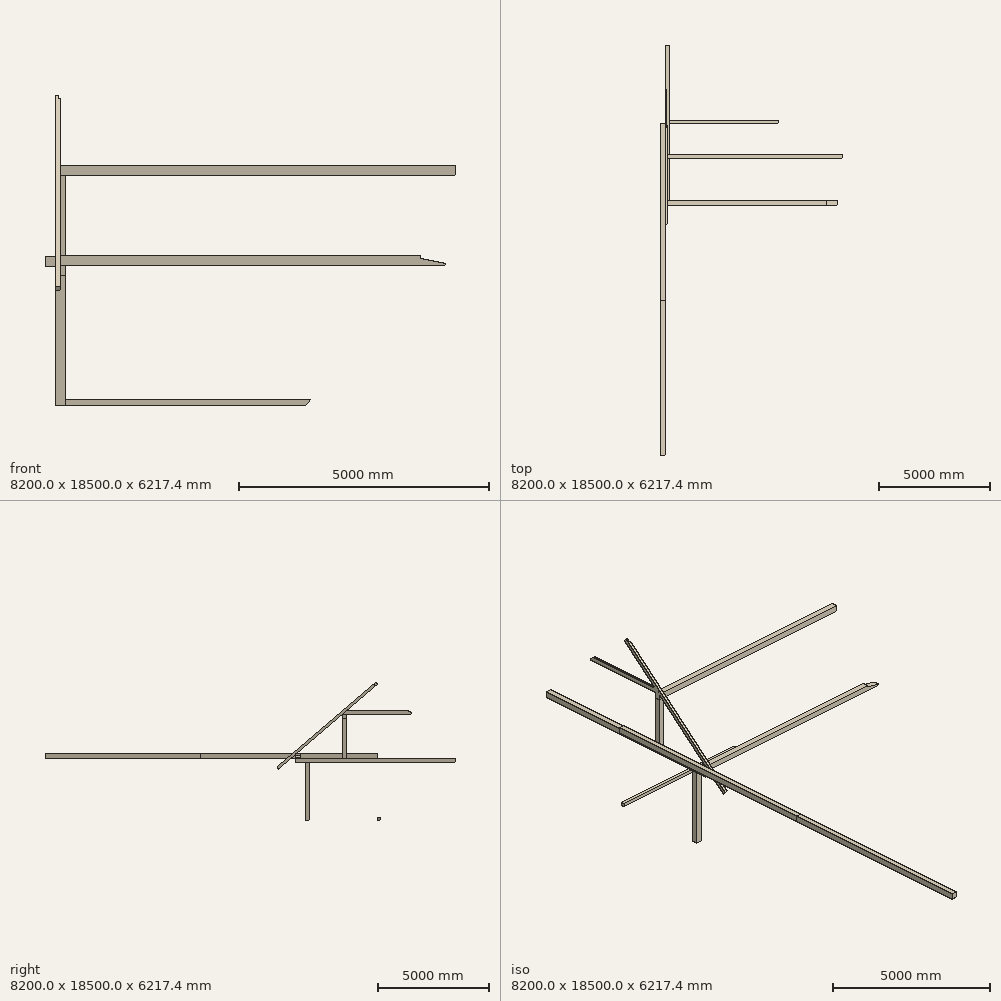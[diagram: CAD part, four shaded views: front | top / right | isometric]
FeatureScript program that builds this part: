
annotation { "Feature Type Name" : "Feature", "Feature Type Description" : "" }
export const myFeature = defineFeature(function(context is Context, id is Id, definition is map)
    precondition{}
    {
        {
            var Q0;
            Q0=qCreatedBy(makeId("Top.planeOp"),FACE);
            var sketch = newSketch(context, id + "F0", { "sketchPlane" : qUnion([Q0])});
            skLineSegment(sketch, "E0.bottom", {"start": v(7000, 3300) * mm, "end": v(-7000, 3300) * mm});
            skLineSegment(sketch, "E0.top", {"start": v(7000, -3300) * mm, "end": v(-7000, -3300) * mm});
            skLineSegment(sketch, "E0.left", {"start": v(7000, 3300) * mm, "end": v(7000, -3300) * mm});
            skLineSegment(sketch, "E0.right", {"start": v(-7000, 3300) * mm, "end": v(-7000, -3300) * mm});
            skPoint(sketch, "E0.middle", {"position": v(0, 0) * mm});
            skSolve(sketch);
        }
        {
            var Q0;
            Q0=qCreatedBy(makeId("Right.planeOp"),FACE);
            var sketch = newSketch(context, id + "F1", { "sketchPlane" : qUnion([Q0])});
            skLineSegment(sketch, "E1", {"start": v(-3286.48, 0) * mm, "end": v(-3286.48, 2600) * mm});
            skLineSegment(sketch, "E2", {"start": v(-3286.48, 2600) * mm, "end": v(-3086.48, 2600) * mm});
            skLineSegment(sketch, "E3", {"start": v(-3086.48, 2600) * mm, "end": v(-3086.48, 0) * mm});
            skLineSegment(sketch, "E4", {"start": v(-3086.48, 0) * mm, "end": v(-3286.48, 0) * mm});
            skSolve(sketch);
        }
        {
            var Q0;
            Q0=makeQuery(id+"F1.imprint","IMPRINT",FACE,{"disambiguationData":[TD([[makeQuery(id+"F1.imprint","IMPRINT",EDGE,{"derivedFrom":sQuery(id+"F1.wireOp",EDGE,"E1")}),-1.0]])]});
            extrude(context, id + "F2", {"entities" : qUnion([Q0]), "depth" : 200 * mm, "offsetDistance" : 25 * mm});
        }
        {
            var Q0;
            Q0=qCreatedBy(makeId("Front.planeOp"),FACE);
            var sketch = newSketch(context, id + "F3", { "sketchPlane" : qUnion([Q0])});
            skLineSegment(sketch, "E5.bottom", {"start": v(-200, 2997.5) * mm, "end": v(0, 2997.5) * mm});
            skLineSegment(sketch, "E5.top", {"start": v(-200, 2797.5) * mm, "end": v(0, 2797.5) * mm});
            skLineSegment(sketch, "E5.left", {"start": v(-200, 2997.5) * mm, "end": v(-200, 2797.5) * mm});
            skLineSegment(sketch, "E5.right", {"start": v(0, 2997.5) * mm, "end": v(0, 2797.5) * mm});
            skSolve(sketch);
        }
        {
            var Q0;
            Q0 = qSketchRegion(id + "F3", true);
            extrude(context, id + "F4", {"entities" : qUnion([Q0]), "depth" : 8000 * mm, "offsetDistance" : 25 * mm});
        }
        {
            var Q0;
            Q0=qCreatedBy(makeId("Right.planeOp"),FACE);
            var sketch = newSketch(context, id + "F5", { "sketchPlane" : qUnion([Q0])});
            skLineSegment(sketch, "E6.bottom", {"start": v(-3700, 0) * mm, "end": v(3500, 0) * mm});
            skLineSegment(sketch, "E6.top", {"start": v(-3700, 2600) * mm, "end": v(3500, 2600) * mm});
            skLineSegment(sketch, "E6.left", {"start": v(-3700, 0) * mm, "end": v(-3700, 2600) * mm});
            skLineSegment(sketch, "E6.right", {"start": v(3500, 0) * mm, "end": v(3500, 2600) * mm});
            skLineSegment(sketch, "E7", {"start": v(-4500, 1914.29) * mm, "end": v(-100, 5685.71) * mm});
            skLineSegment(sketch, "E8", {"start": v(-100, 5685.71) * mm, "end": v(4300, 1914.29) * mm});
            skPoint(sketch, "E9", {"position": v(-100, 2600) * mm});
            skLineSegment(sketch, "E10.top", {"start": v(-3700, 3000) * mm, "end": v(3500, 3000) * mm});
            skLineSegment(sketch, "E10.left", {"start": v(-3700, 2600) * mm, "end": v(-3700, 3000) * mm});
            skLineSegment(sketch, "E10.right", {"start": v(3500, 2600) * mm, "end": v(3500, 3000) * mm});
            skLineSegment(sketch, "E11", {"start": v(-4500, 2314.29) * mm, "end": v(-100, 6085.71) * mm});
            skLineSegment(sketch, "E12", {"start": v(-100, 6085.71) * mm, "end": v(4300, 2314.29) * mm});
            skLineSegment(sketch, "E13.bottom", {"start": v(-1600, 4800) * mm, "end": v(1400, 4800) * mm});
            skLineSegment(sketch, "E13.top", {"start": v(-1600, 2800) * mm, "end": v(1400, 2800) * mm});
            skLineSegment(sketch, "E13.left", {"start": v(-1600, 4800) * mm, "end": v(-1600, 2800) * mm});
            skLineSegment(sketch, "E13.right", {"start": v(1400, 4800) * mm, "end": v(1400, 2800) * mm});
            skPoint(sketch, "E14", {"position": v(-100, 2800) * mm});
            skSolve(sketch);
        }
        {
            var Q0;
            Q0=makeQuery(id+"F4.opExtrude","CAP_FACE",FACE,{"disambiguationData":[OSD([sQuery(id+"F3.wireOp",EDGE,"E5.bottom"),sQuery(id+"F3.wireOp",EDGE,"E5.top"),sQuery(id+"F3.wireOp",EDGE,"E5.left"),sQuery(id+"F3.wireOp",EDGE,"E5.right")])],"isStart":false});
            extrude(context, id + "F6", {"entities" : qUnion([Q0]), "depth" : 7000 * mm, "offsetDistance" : 25 * mm});
        }
        {
            var Q0;
            Q0=qCreatedBy(makeId("Right.planeOp"),FACE);
            var sketch = newSketch(context, id + "F7", { "sketchPlane" : qUnion([Q0])});
            skLineSegment(sketch, "E15.bottom", {"start": v(0, 0) * mm, "end": v(120, 0) * mm});
            skLineSegment(sketch, "E15.top", {"start": v(0, 120) * mm, "end": v(120, 120) * mm});
            skLineSegment(sketch, "E15.left", {"start": v(0, 0) * mm, "end": v(0, 120) * mm});
            skLineSegment(sketch, "E15.right", {"start": v(120, 0) * mm, "end": v(120, 120) * mm});
            skSolve(sketch);
        }
        {
            var Q0;
            Q0 = qSketchRegion(id + "F7", true);
            extrude(context, id + "F8", {"entities" : qUnion([Q0]), "depth" : 5100 * mm, "offsetDistance" : 25 * mm});
        }
        {
            var Q0;
            Q0=makeQuery(id+"F8.opExtrude","SWEPT_FACE",FACE,{"disambiguationData":[OSD([sQuery(id+"F7.wireOp",EDGE,"E15.right")])]});
            var sketch = newSketch(context, id + "F9", { "sketchPlane" : qUnion([Q0])});
            skLineSegment(sketch, "E16", {"start": v(-5100, 120) * mm, "end": v(-5015.98, 0) * mm});
            skSolve(sketch);
        }
        {
            var Q0;
            {var subQ0=sQuery(id+"F9.wireOp",EDGE,"E16");Q0=makeQuery(id+"F9.imprint","IMPRINT",FACE,{"disambiguationData":[TD([[makeQuery(id+"F9.imprint","IMPRINT",EDGE,{"derivedFrom":subQ0}),-1.0]])]});}
            extrude(context, id + "F10", {"entities" : qUnion([Q0]), "operationType" : NewBodyOperationType.REMOVE, "endBound" : BoundingType.THROUGH_ALL, "oppositeDirection" : true, "depth" : 25 * mm, "offsetDistance" : 25 * mm});
        }
        {
            var Q0;
            Q0=qCreatedBy(makeId("Right.planeOp"),FACE);
            var sketch = newSketch(context, id + "F11", { "sketchPlane" : qUnion([Q0])});
            skLineSegment(sketch, "E17.0", {"start": v(-4486.98, 1899.1) * mm, "end": v(-84.63, 5672.54) * mm});
            skLineSegment(sketch, "E18.0", {"start": v(-4565.08, 1990.21) * mm, "end": v(-176.83, 5751.57) * mm, "construction": true});
            skLineSegment(sketch, "E19", {"start": v(-4565.08, 1990.21) * mm, "end": v(-4486.98, 1899.1) * mm});
            skLineSegment(sketch, "E20", {"start": v(-176.83, 5751.57) * mm, "end": v(-84.63, 5672.54) * mm, "construction": true});
            skPoint(sketch, "E21.0", {"position": v(-3700, 2600) * mm});
            skLineSegment(sketch, "E22", {"start": v(-3700, 2600) * mm, "end": v(-3700, 2573.66) * mm});
            skLineSegment(sketch, "E23", {"start": v(-3700, 2600) * mm, "end": v(-3669.27, 2600) * mm});
            skLineSegment(sketch, "E24", {"start": v(-100, 5817.42) * mm, "end": v(-7.8, 5738.4) * mm});
            skLineSegment(sketch, "E25", {"start": v(-176.83, 5751.57) * mm, "end": v(-100, 5817.42) * mm});
            skLineSegment(sketch, "E26", {"start": v(-7.8, 5738.4) * mm, "end": v(-84.63, 5672.54) * mm});
            skLineSegment(sketch, "E27.0", {"start": v(-4486.98, 2299.1) * mm, "end": v(-7.8, 6138.4) * mm});
            skLineSegment(sketch, "E28.0", {"start": v(-4565.08, 2390.21) * mm, "end": v(-100, 6217.42) * mm});
            skLineSegment(sketch, "E29", {"start": v(-4565.08, 2390.21) * mm, "end": v(-4486.98, 2299.1) * mm});
            skLineSegment(sketch, "E30", {"start": v(-100, 6217.42) * mm, "end": v(-7.8, 6138.4) * mm});
            skPoint(sketch, "E31.0", {"position": v(-3700, 3000) * mm});
            skLineSegment(sketch, "E32", {"start": v(-3700, 3000) * mm, "end": v(-3669.27, 3000) * mm});
            skLineSegment(sketch, "E33", {"start": v(-3700, 3000) * mm, "end": v(-3700, 2973.66) * mm});
            skSolve(sketch);
        }
        {
            var Q0;
            Q0=makeQuery(id+"F11.imprint","IMPRINT",FACE,{"disambiguationData":[TD([[makeQuery(id+"F11.imprint","IMPRINT",EDGE,{"derivedFrom":sQuery(id+"F11.wireOp",EDGE,"E28.0")}),-1.0]])]});
            extrude(context, id + "F12", {"entities" : qUnion([Q0]), "depth" : 100 * mm, "offsetDistance" : 25 * mm});
        }
        {
            var Q0;
            Q0=makeQuery(id+"F12.opExtrude","CAP_FACE",FACE,{"disambiguationData":[OSD([sQuery(id+"F11.wireOp",EDGE,"E27.0"),sQuery(id+"F11.wireOp",EDGE,"E28.0"),sQuery(id+"F11.wireOp",EDGE,"E29"),sQuery(id+"F11.wireOp",EDGE,"E30"),sQuery(id+"F11.wireOp",EDGE,"E32"),sQuery(id+"F11.wireOp",EDGE,"E33")])],"isStart":false});
            var sketch = newSketch(context, id + "F13", { "sketchPlane" : qUnion([Q0])});
            skLineSegment(sketch, "E34", {"start": v(-192.2, 6138.4) * mm, "end": v(-100, 6059.37) * mm});
            skSolve(sketch);
        }
        {
            var Q0;
            {var subQ0=sQuery(id+"F13.wireOp",EDGE,"E34");Q0=makeQuery(id+"F13.imprint","IMPRINT",FACE,{"disambiguationData":[TD([[makeQuery(id+"F13.imprint","IMPRINT",EDGE,{"derivedFrom":subQ0}),1.0]])]});}
            extrude(context, id + "F14", {"entities" : qUnion([Q0]), "operationType" : NewBodyOperationType.REMOVE, "oppositeDirection" : true, "depth" : 50 * mm, "offsetDistance" : 25 * mm});
        }
        {
            var Q0;
            Q0=qCreatedBy(makeId("Right.planeOp"),FACE);
            var sketch = newSketch(context, id + "F15", { "sketchPlane" : qUnion([Q0])});
            skPoint(sketch, "E35.0", {"position": v(-3700, 2600) * mm});
            skPoint(sketch, "E35.1", {"position": v(3500, 2600) * mm});
            skLineSegment(sketch, "E36.bottom", {"start": v(-3700, 2600) * mm, "end": v(3500, 2600) * mm});
            skLineSegment(sketch, "E36.top", {"start": v(-3700, 2800) * mm, "end": v(3500, 2800) * mm});
            skLineSegment(sketch, "E36.left", {"start": v(-3700, 2600) * mm, "end": v(-3700, 2800) * mm});
            skLineSegment(sketch, "E36.right", {"start": v(3500, 2600) * mm, "end": v(3500, 2800) * mm});
            skSolve(sketch);
        }
        {
            var Q0;
            Q0 = qSketchRegion(id + "F15", true);
            extrude(context, id + "F16", {"entities" : qUnion([Q0]), "depth" : 200 * mm, "offsetDistance" : 25 * mm});
        }
        {
            var Q0;
            Q0=qCreatedBy(makeId("Right.planeOp"),FACE);
            var sketch = newSketch(context, id + "F17", { "sketchPlane" : qUnion([Q0])});
            skPoint(sketch, "E37.0", {"position": v(-3700, 2800) * mm});
            skLineSegment(sketch, "E38.bottom", {"start": v(-3700, 2800) * mm, "end": v(-3500, 2800) * mm});
            skLineSegment(sketch, "E38.top", {"start": v(-3700, 3000) * mm, "end": v(-3500, 3000) * mm});
            skLineSegment(sketch, "E38.left", {"start": v(-3700, 2800) * mm, "end": v(-3700, 3000) * mm});
            skLineSegment(sketch, "E38.right", {"start": v(-3500, 2800) * mm, "end": v(-3500, 3000) * mm});
            skSolve(sketch);
        }
        {
            var Q0;
            Q0 = qSketchRegion(id + "F17", true);
            extrude(context, id + "F18", {"entities" : qUnion([Q0]), "depth" : 7800 * mm, "offsetDistance" : 25 * mm});
        }
        {
            var Q0;
            Q0=makeQuery(id+"F18.opExtrude","SWEPT_FACE",FACE,{"disambiguationData":[OSD([sQuery(id+"F17.wireOp",EDGE,"E38.left")])]});
            var sketch = newSketch(context, id + "F19", { "sketchPlane" : qUnion([Q0])});
            skLineSegment(sketch, "E39", {"start": v(7800, 2800) * mm, "end": v(7800, 2850) * mm});
            skLineSegment(sketch, "E40", {"start": v(7800, 2850) * mm, "end": v(7300, 2950) * mm});
            skLineSegment(sketch, "E41", {"start": v(7300, 2950) * mm, "end": v(7300, 3000) * mm});
            skSolve(sketch);
        }
        {
            var Q0;
            {var subQ0=sQuery(id+"F19.wireOp",EDGE,"E40");Q0=makeQuery(id+"F19.imprint","IMPRINT",FACE,{"disambiguationData":[TD([[makeQuery(id+"F19.imprint","IMPRINT",EDGE,{"derivedFrom":subQ0}),-1.0]])]});}
            extrude(context, id + "F20", {"entities" : qUnion([Q0]), "operationType" : NewBodyOperationType.REMOVE, "endBound" : BoundingType.THROUGH_ALL, "oppositeDirection" : true, "depth" : 25 * mm, "offsetDistance" : 25 * mm});
        }
        {
            var Q0;
            Q0=qCreatedBy(makeId("Right.planeOp"),FACE);
            var sketch = newSketch(context, id + "F21", { "sketchPlane" : qUnion([Q0])});
            skLineSegment(sketch, "E42.0", {"start": v(-3700, 3000) * mm, "end": v(3500, 3000) * mm});
            skLineSegment(sketch, "E43.0", {"start": v(-3669.27, 3000) * mm, "end": v(-100, 6059.37) * mm});
            skLineSegment(sketch, "E44", {"start": v(-1335.93, 3000) * mm, "end": v(-1335.93, 5000) * mm});
            skLineSegment(sketch, "E45.0", {"start": v(-3700, 2800) * mm, "end": v(3500, 2800) * mm});
            skLineSegment(sketch, "E46", {"start": v(-1569.27, 2800) * mm, "end": v(-1569.27, 4800) * mm});
            skSolve(sketch);
        }
        {
            var Q0;
            Q0=makeQuery(id+"F12.opExtrude","CAP_FACE",FACE,{"disambiguationData":[OSD([sQuery(id+"F11.wireOp",EDGE,"E27.0"),sQuery(id+"F11.wireOp",EDGE,"E28.0"),sQuery(id+"F11.wireOp",EDGE,"E29"),sQuery(id+"F11.wireOp",EDGE,"E30"),sQuery(id+"F11.wireOp",EDGE,"E32"),sQuery(id+"F11.wireOp",EDGE,"E33")])],"isStart":false});
            var sketch = newSketch(context, id + "F22", { "sketchPlane" : qUnion([Q0])});
            skPoint(sketch, "E47.0", {"position": v(-1600, 4800) * mm});
            skPoint(sketch, "E47.1", {"position": v(-1569.27, 4800) * mm});
            skLineSegment(sketch, "E48", {"start": v(-1569.27, 4800) * mm, "end": v(-1600, 4800) * mm});
            skLineSegment(sketch, "E49", {"start": v(-1600, 4773.66) * mm, "end": v(-1600, 4800) * mm});
            skLineSegment(sketch, "E50", {"start": v(-1600, 4773.66) * mm, "end": v(-1569.27, 4800) * mm});
            skCircle(sketch, "E51", {"center": v(-1573.96, 4875) * mm, "radius": 7.5 * mm});
            skLineSegment(sketch, "E52", {"start": v(-1613.01, 4920.56) * mm, "end": v(-1534.92, 4829.44) * mm, "construction": true});
            skLineSegment(sketch, "E53.bottom", {"start": v(-1700, 4800) * mm, "end": v(-1378.17, 4800) * mm, "construction": true});
            skLineSegment(sketch, "E53.top", {"start": v(-1700, 4950) * mm, "end": v(-1378.17, 4950) * mm, "construction": true});
            skLineSegment(sketch, "E53.left", {"start": v(-1700, 4800) * mm, "end": v(-1700, 4950) * mm, "construction": true});
            skLineSegment(sketch, "E53.right", {"start": v(-1378.17, 4800) * mm, "end": v(-1378.17, 4950) * mm, "construction": true});
            skLineSegment(sketch, "E54", {"start": v(-1573.96, 4950) * mm, "end": v(-1573.96, 4800) * mm, "construction": true});
            skSolve(sketch);
        }
        {
            var Q0;
            Q0 = qSketchRegion(id + "F22", true);
            extrude(context, id + "F23", {"entities" : qUnion([Q0]), "operationType" : NewBodyOperationType.REMOVE, "endBound" : BoundingType.THROUGH_ALL, "oppositeDirection" : true, "depth" : 25 * mm, "offsetDistance" : 25 * mm});
        }
        {
            var Q0;
            Q0=qCreatedBy(makeId("Right.planeOp"),FACE);
            var sketch = newSketch(context, id + "F24", { "sketchPlane" : qUnion([Q0])});
            skPoint(sketch, "E55.0", {"position": v(-1600, 4800) * mm});
            skLineSegment(sketch, "E56.bottom", {"start": v(-1600, 4800) * mm, "end": v(-1400, 4800) * mm});
            skLineSegment(sketch, "E56.top", {"start": v(-1600, 4600) * mm, "end": v(-1400, 4600) * mm});
            skLineSegment(sketch, "E56.left", {"start": v(-1600, 4800) * mm, "end": v(-1600, 4600) * mm});
            skLineSegment(sketch, "E56.right", {"start": v(-1400, 4800) * mm, "end": v(-1400, 4600) * mm});
            skSolve(sketch);
        }
        {
            var Q0;
            Q0 = qSketchRegion(id + "F24", true);
            extrude(context, id + "F25", {"entities" : qUnion([Q0]), "depth" : 8000 * mm, "offsetDistance" : 25 * mm});
        }
        {
            var Q0;
            Q0=qCreatedBy(makeId("Right.planeOp"),FACE);
            var sketch = newSketch(context, id + "F26", { "sketchPlane" : qUnion([Q0])});
            skPoint(sketch, "E57.0", {"position": v(-1400, 4600) * mm});
            skPoint(sketch, "E58.0", {"position": v(-1600, 2800) * mm});
            skLineSegment(sketch, "E59.bottom", {"start": v(-1400, 4600) * mm, "end": v(-1600, 4600) * mm});
            skLineSegment(sketch, "E59.top", {"start": v(-1400, 2800) * mm, "end": v(-1600, 2800) * mm});
            skLineSegment(sketch, "E59.left", {"start": v(-1400, 4600) * mm, "end": v(-1400, 2800) * mm});
            skLineSegment(sketch, "E59.right", {"start": v(-1600, 4600) * mm, "end": v(-1600, 2800) * mm});
            skSolve(sketch);
        }
        {
            var Q0;
            Q0 = qSketchRegion(id + "F26", true);
            extrude(context, id + "F27", {"entities" : qUnion([Q0]), "depth" : 200 * mm, "offsetDistance" : 25 * mm});
        }
        {
            var Q0;
            Q0=qCreatedBy(makeId("Right.planeOp"),FACE);
            var sketch = newSketch(context, id + "F28", { "sketchPlane" : qUnion([Q0])});
            skPoint(sketch, "E60.0", {"position": v(-1600, 4800) * mm});
            skLineSegment(sketch, "E61.bottom", {"start": v(-1700, 4800) * mm, "end": v(-100, 4800) * mm});
            skLineSegment(sketch, "E61.top", {"start": v(-1700, 4950) * mm, "end": v(-100, 4950) * mm});
            skLineSegment(sketch, "E61.left", {"start": v(-1700, 4800) * mm, "end": v(-1700, 4950) * mm});
            skLineSegment(sketch, "E61.right", {"start": v(-100, 4800) * mm, "end": v(-100, 4950) * mm});
            skLineSegment(sketch, "E62", {"start": v(-1578.66, 4950) * mm, "end": v(-1700, 4846) * mm});
            skCircle(sketch, "E63.0", {"center": v(-1573.96, 4875) * mm, "radius": 7.5 * mm});
            skSolve(sketch);
        }
        {
            var Q0;
            {var subQ1=sQuery(id+"F28.wireOp",EDGE,"E61.bottom");Q0=makeQuery(id+"F28.imprint","IMPRINT",FACE,{"disambiguationData":[TD([[makeQuery(id+"F28.imprint","IMPRINT",EDGE,{"derivedFrom":subQ1}),1.0]])]});}
            extrude(context, id + "F29", {"entities" : qUnion([Q0]), "depth" : 50 * mm, "offsetDistance" : 25 * mm});
        }
        {
            var Q0;
            Q0=makeQuery(id+"F29.opExtrude","SWEPT_BODY",BODY,{"disambiguationData":[OSD([sQuery(id+"F28.wireOp",EDGE,"E61.bottom"),sQuery(id+"F28.wireOp",EDGE,"E61.top"),sQuery(id+"F28.wireOp",EDGE,"E61.left"),sQuery(id+"F28.wireOp",EDGE,"E61.right"),sQuery(id+"F28.wireOp",EDGE,"E62")])]});
            var Q1;
            Q1=makeQuery(id+"F29.opExtrude","SWEPT_FACE",FACE,{"disambiguationData":[OSD([sQuery(id+"F28.wireOp",EDGE,"E61.right")])]});
            mirror(context, id + "F30", {"operationType" : NewBodyOperationType.ADD, "entities" : qUnion([Q0]), "mirrorPlane" : qUnion([Q1])});
        }
    });
